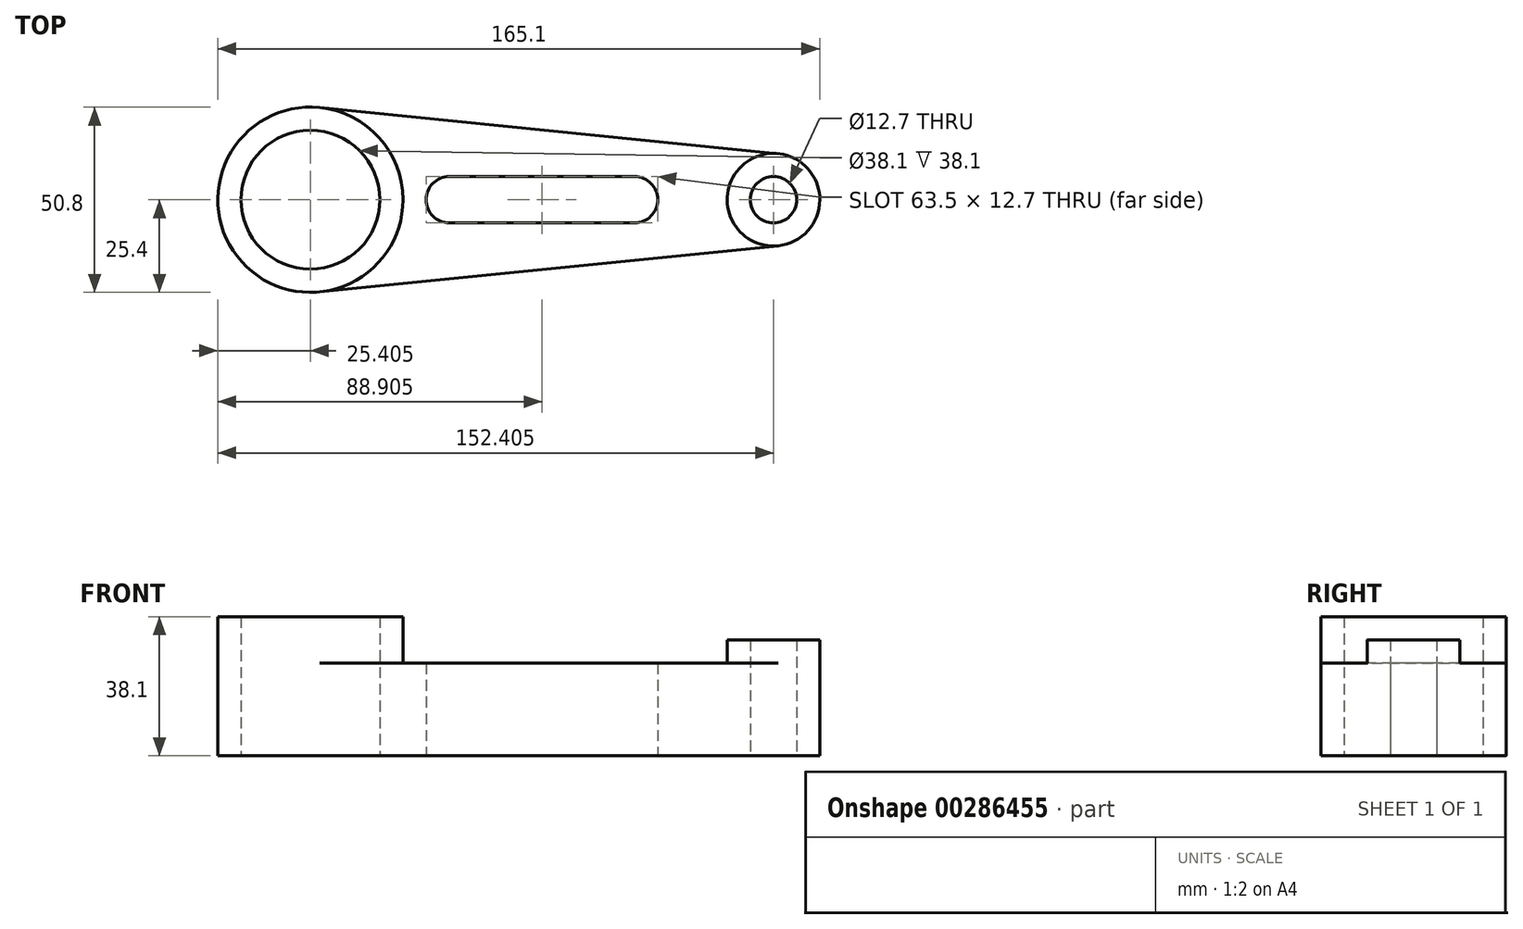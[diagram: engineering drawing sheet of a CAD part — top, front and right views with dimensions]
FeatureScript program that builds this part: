
annotation { "Feature Type Name" : "Feature", "Feature Type Description" : "" }
export const myFeature = defineFeature(function(context is Context, id is Id, definition is map)
    precondition{}
    {
        {
            var Q0;
            Q0=qCreatedBy(makeId("Top.planeOp"),FACE);
            var sketch = newSketch(context, id + "F0", { "sketchPlane" : qUnion([Q0])});
            skCircle(sketch, "E0", {"center": v(-52.53, 0) * mm, "radius": 19.05 * mm});
            skCircle(sketch, "E1", {"center": v(-52.53, 0) * mm, "radius": 25.4 * mm});
            skLineSegment(sketch, "E2", {"start": v(-49.99, 25.27) * mm, "end": v(75.74, 12.64) * mm});
            skLineSegment(sketch, "E3", {"start": v(-49.99, -25.27) * mm, "end": v(75.74, -12.64) * mm});
            skCircle(sketch, "E4", {"center": v(74.47, 0) * mm, "radius": 12.7 * mm});
            skCircle(sketch, "E5", {"center": v(74.47, 0) * mm, "radius": 6.35 * mm});
            skArc(sketch, "E6", {"start": v(-14.43, 6.35) * mm, "mid": v(-20.78, 0) * mm, "end": v(-14.43, -6.35) * mm});
            skArc(sketch, "E7", {"start": v(36.37, -6.35) * mm, "mid": v(42.72, 0) * mm, "end": v(36.37, 6.35) * mm});
            skLineSegment(sketch, "E8", {"start": v(-14.43, 6.35) * mm, "end": v(36.37, 6.35) * mm});
            skLineSegment(sketch, "E9", {"start": v(-14.43, -6.35) * mm, "end": v(36.37, -6.35) * mm});
            skLineSegment(sketch, "E10", {"start": v(-52.53, 0) * mm, "end": v(201.47, 0) * mm, "construction": true});
            skSolve(sketch);
        }
        {
            var Q0;
            {var subQ1=sQuery(id+"F0.wireOp",EDGE,"E2");Q0=makeQuery(id+"F0.imprint","IMPRINT",FACE,{"disambiguationData":[TD([[makeQuery(id+"F0.imprint","IMPRINT",EDGE,{"derivedFrom":subQ1}),-1.0]])]});}
            var Q1;
            Q1=makeQuery(id+"F0.imprint","IMPRINT",FACE,{"disambiguationData":[TD([[makeQuery(id+"F0.imprint","IMPRINT",EDGE,{"derivedFrom":sQuery(id+"F0.wireOp",EDGE,"E0")}),-1.0]])]});
            var Q2;
            Q2=makeQuery(id+"F0.imprint","IMPRINT",FACE,{"disambiguationData":[TD([[makeQuery(id+"F0.imprint","IMPRINT",EDGE,{"derivedFrom":sQuery(id+"F0.wireOp",EDGE,"E5")}),-1.0]])]});
            extrude(context, id + "F1", {"entities" : qUnion([Q0, Q1, Q2]), "depth" : 25.4 * mm});
        }
        {
            var Q0;
            Q0=makeQuery(id+"F0.imprint","IMPRINT",FACE,{"disambiguationData":[TD([[makeQuery(id+"F0.imprint","IMPRINT",EDGE,{"derivedFrom":sQuery(id+"F0.wireOp",EDGE,"E0")}),-1.0]])]});
            extrude(context, id + "F2", {"entities" : qUnion([Q0]), "operationType" : NewBodyOperationType.ADD, "depth" : 38.1 * mm});
        }
        {
            var Q0;
            Q0=makeQuery(id+"F0.imprint","IMPRINT",FACE,{"disambiguationData":[TD([[makeQuery(id+"F0.imprint","IMPRINT",EDGE,{"derivedFrom":sQuery(id+"F0.wireOp",EDGE,"E5")}),-1.0]])]});
            extrude(context, id + "F3", {"entities" : qUnion([Q0]), "operationType" : NewBodyOperationType.ADD, "depth" : 31.75 * mm});
        }
    });
